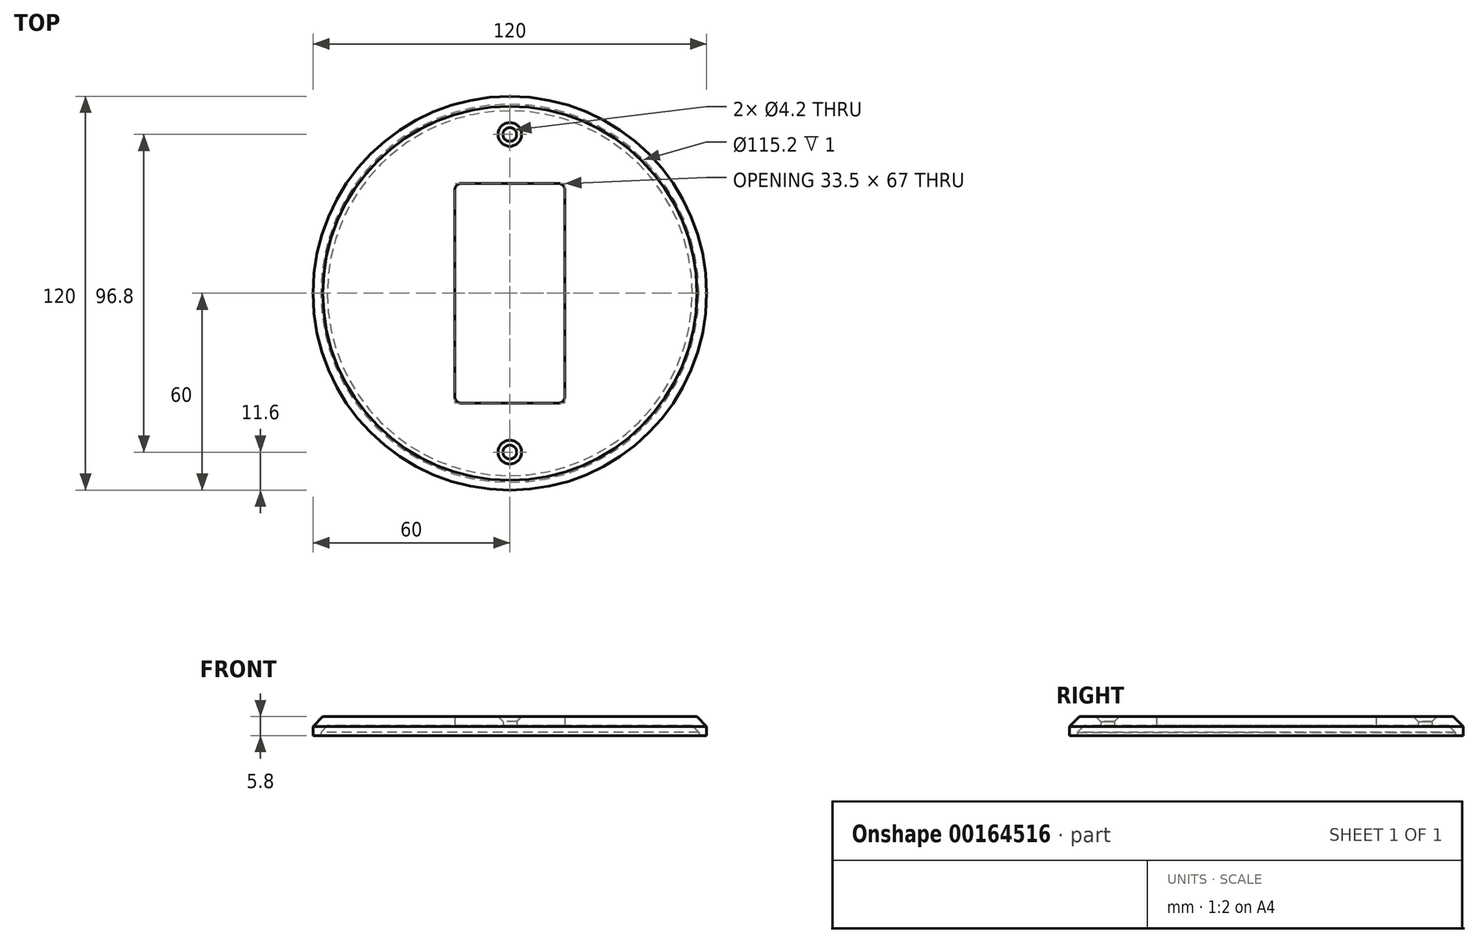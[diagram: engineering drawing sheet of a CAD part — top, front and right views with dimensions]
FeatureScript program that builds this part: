
annotation { "Feature Type Name" : "Feature", "Feature Type Description" : "" }
export const myFeature = defineFeature(function(context is Context, id is Id, definition is map)
    precondition{}
    {
        {
            var Q0;
            Q0=qCreatedBy(makeId("Top.planeOp"),FACE);
            var sketch = newSketch(context, id + "F0", { "sketchPlane" : qUnion([Q0])});
            skCircle(sketch, "E0", {"center": v(0, 0) * mm, "radius": 60 * mm});
            skLineSegment(sketch, "E1.bottom", {"start": v(14.75, 33.5) * mm, "end": v(-14.75, 33.5) * mm});
            skLineSegment(sketch, "E1.top", {"start": v(14.75, -33.5) * mm, "end": v(-14.75, -33.5) * mm});
            skLineSegment(sketch, "E1.left", {"start": v(16.75, 31.5) * mm, "end": v(16.75, -31.5) * mm});
            skLineSegment(sketch, "E1.right", {"start": v(-16.75, 31.5) * mm, "end": v(-16.75, -31.5) * mm});
            skCircle(sketch, "E2", {"center": v(0, 48.4) * mm, "radius": 2.1 * mm});
            skCircle(sketch, "E3", {"center": v(0, -48.4) * mm, "radius": 2.1 * mm});
            skPoint(sketch, "E4.visualSharp", {"position": v(-16.75, 33.5) * mm});
            skArc(sketch, "E4.filletArc", {"start": v(-14.75, 33.5) * mm, "mid": v(-16.16, 32.91) * mm, "end": v(-16.75, 31.5) * mm});
            skPoint(sketch, "E5.visualSharp", {"position": v(16.75, 33.5) * mm});
            skArc(sketch, "E5.filletArc", {"start": v(16.75, 31.5) * mm, "mid": v(16.16, 32.91) * mm, "end": v(14.75, 33.5) * mm});
            skPoint(sketch, "E6.visualSharp", {"position": v(16.75, -33.5) * mm});
            skArc(sketch, "E6.filletArc", {"start": v(14.75, -33.5) * mm, "mid": v(16.16, -32.91) * mm, "end": v(16.75, -31.5) * mm});
            skPoint(sketch, "E7.visualSharp", {"position": v(-16.75, -33.5) * mm});
            skArc(sketch, "E7.filletArc", {"start": v(-16.75, -31.5) * mm, "mid": v(-16.16, -32.91) * mm, "end": v(-14.75, -33.5) * mm});
            skCircle(sketch, "E8", {"center": v(0, 0) * mm, "radius": 57.6 * mm});
            skSolve(sketch);
        }
        {
            var Q0;
            Q0=makeQuery(id+"F0.imprint","IMPRINT",FACE,{"disambiguationData":[TD([[makeQuery(id+"F0.imprint","IMPRINT",EDGE,{"derivedFrom":sQuery(id+"F0.wireOp",EDGE,"E0")}),1.0]])]});
            var Q1;
            Q1=makeQuery(id+"F0.imprint","IMPRINT",FACE,{"disambiguationData":[TD([[makeQuery(id+"F0.imprint","IMPRINT",EDGE,{"derivedFrom":sQuery(id+"F0.wireOp",EDGE,"E1.bottom")}),-1.0]])]});
            extrude(context, id + "F1", {"entities" : qUnion([Q0, Q1]), "depth" : 5.8 * mm});
        }
        {
            var Q0;
            Q0=makeQuery(id+"F1.opExtrude","CAP_EDGE",EDGE,{"disambiguationData":[OSD([sQuery(id+"F0.wireOp",EDGE,"E0")])],"isStart":false});
            chamfer(context, id + "F2", {"entities" : qUnion([Q0]), "width" : 3 * mm, "tangentPropagation" : true});
        }
        {
            var Q0;
            Q0=makeQuery(id+"F0.imprint","IMPRINT",FACE,{"disambiguationData":[TD([[makeQuery(id+"F0.imprint","IMPRINT",EDGE,{"derivedFrom":sQuery(id+"F0.wireOp",EDGE,"E1.bottom")}),-1.0]])]});
            extrude(context, id + "F3", {"entities" : qUnion([Q0]), "operationType" : NewBodyOperationType.REMOVE, "depth" : 3 * mm});
        }
        {
            var Q0;
            Q0=makeQuery(id+"F3.boolean.opBoolean","COPY",EDGE,{"derivedFrom":makeQuery(id+"F3.opExtrude","CAP_EDGE",EDGE,{"disambiguationData":[OSD([sQuery(id+"F0.wireOp",EDGE,"E8")])],"isStart":false})});
            chamfer(context, id + "F4", {"entities" : qUnion([Q0]), "width" : 2 * mm, "tangentPropagation" : true});
        }
        {
            var Q0;
            Q0=makeQuery(id+"F1.opExtrude","CAP_EDGE",EDGE,{"disambiguationData":[OSD([sQuery(id+"F0.wireOp",EDGE,"E3")])],"isStart":false});
            var Q1;
            Q1=makeQuery(id+"F1.opExtrude","CAP_EDGE",EDGE,{"disambiguationData":[OSD([sQuery(id+"F0.wireOp",EDGE,"E2")])],"isStart":false});
            chamfer(context, id + "F5", {"entities" : qUnion([Q0, Q1]), "width" : 1.5 * mm, "tangentPropagation" : true});
        }
    });
